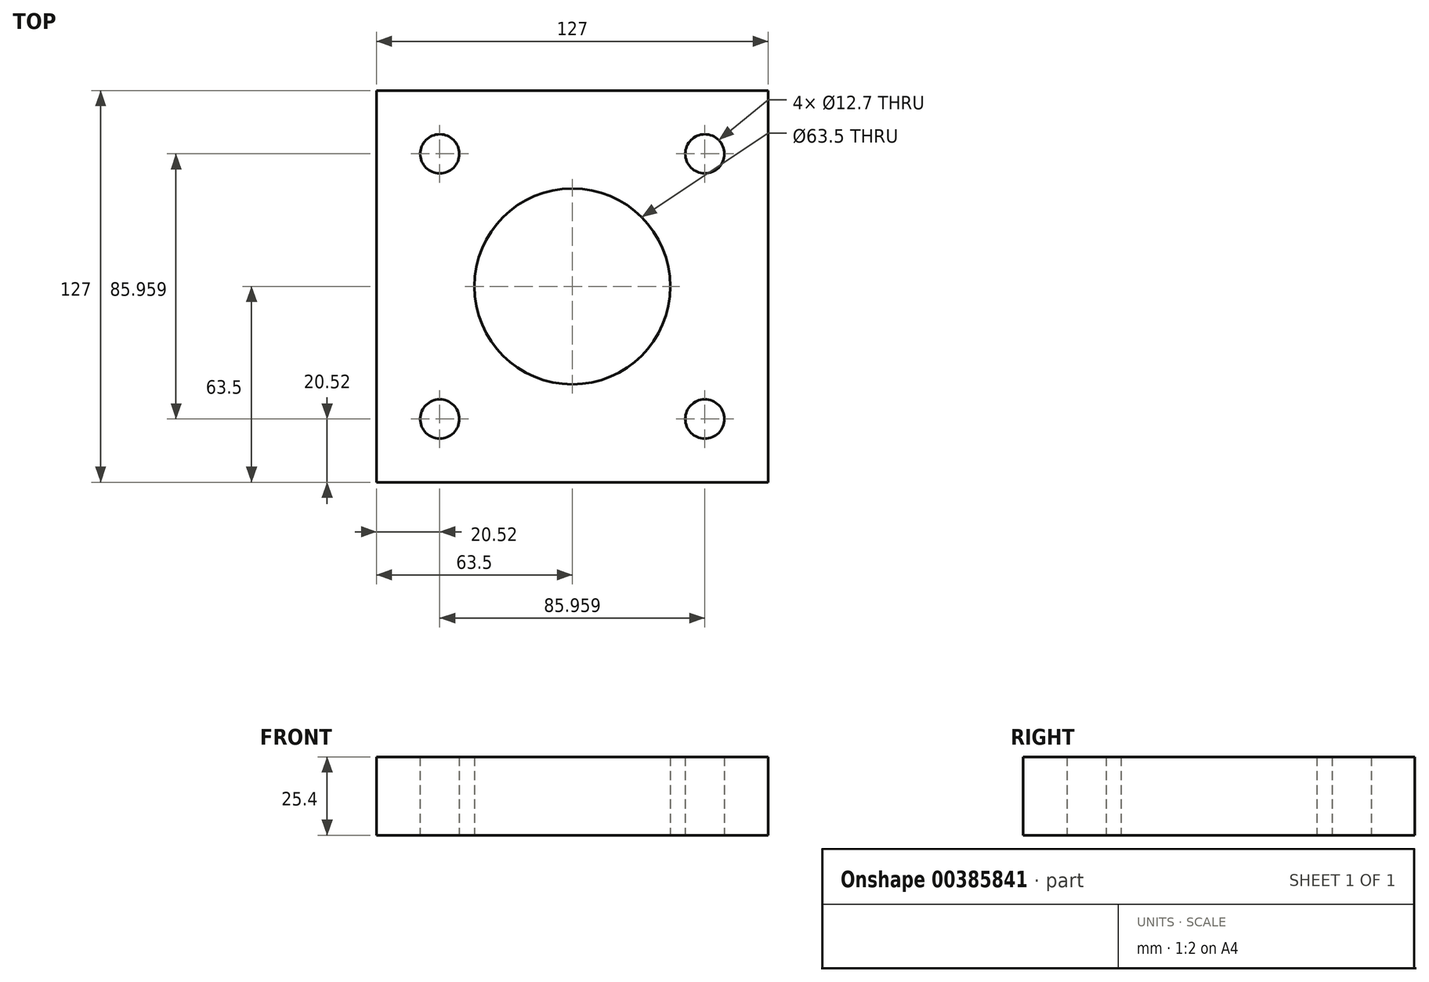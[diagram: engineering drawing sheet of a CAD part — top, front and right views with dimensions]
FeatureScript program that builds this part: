
annotation { "Feature Type Name" : "Feature", "Feature Type Description" : "" }
export const myFeature = defineFeature(function(context is Context, id is Id, definition is map)
    precondition{}
    {
        {
            var Q0;
            Q0=qCreatedBy(makeId("Top.planeOp"),FACE);
            var sketch = newSketch(context, id + "F0", { "sketchPlane" : qUnion([Q0])});
            skLineSegment(sketch, "E0.bottom", {"start": v(-63.5, 63.5) * mm, "end": v(63.5, 63.5) * mm});
            skLineSegment(sketch, "E0.top", {"start": v(-63.5, -63.5) * mm, "end": v(63.5, -63.5) * mm});
            skLineSegment(sketch, "E0.left", {"start": v(-63.5, 63.5) * mm, "end": v(-63.5, -63.5) * mm});
            skLineSegment(sketch, "E0.right", {"start": v(63.5, 63.5) * mm, "end": v(63.5, -63.5) * mm});
            skCircle(sketch, "E1", {"center": v(-42.98, 42.98) * mm, "radius": 6.35 * mm});
            skCircle(sketch, "E2", {"center": v(42.98, 42.98) * mm, "radius": 6.35 * mm});
            skCircle(sketch, "E3", {"center": v(42.98, -42.98) * mm, "radius": 6.35 * mm});
            skCircle(sketch, "E4", {"center": v(-42.98, -42.98) * mm, "radius": 6.35 * mm});
            skCircle(sketch, "E5", {"center": v(0, 0) * mm, "radius": 31.75 * mm});
            skSolve(sketch);
        }
        {
            var Q0;
            Q0=makeQuery(id+"F0.imprint","IMPRINT",FACE,{"disambiguationData":[TD([[makeQuery(id+"F0.imprint","IMPRINT",EDGE,{"derivedFrom":sQuery(id+"F0.wireOp",EDGE,"E0.bottom")}),-1.0]])]});
            extrude(context, id + "F1", {"entities" : qUnion([Q0]), "depth" : 25.4 * mm});
        }
    });
